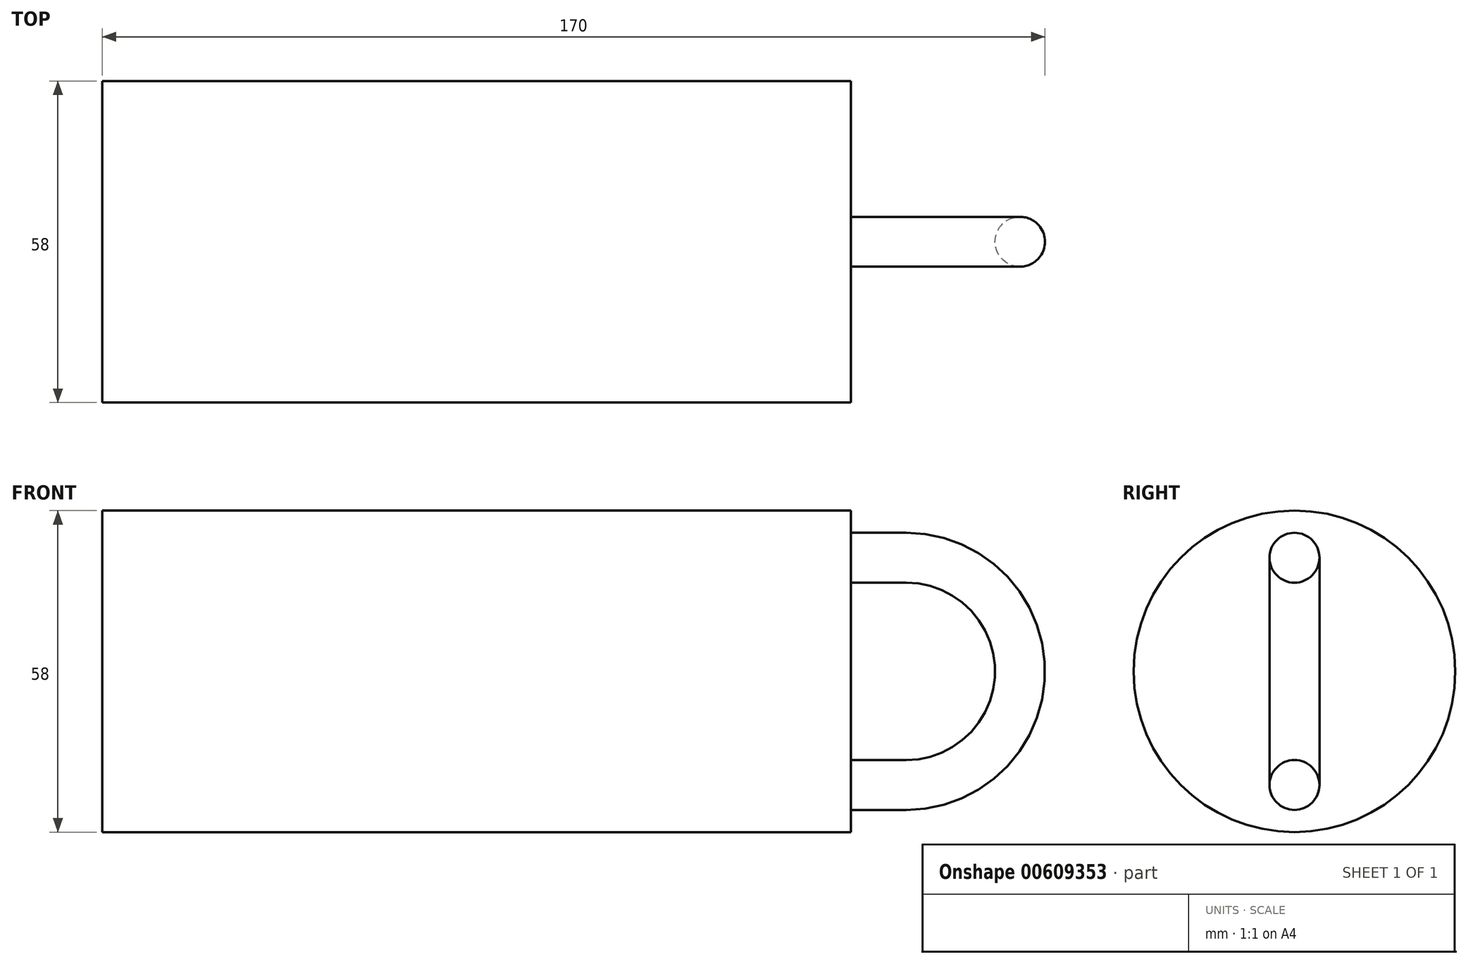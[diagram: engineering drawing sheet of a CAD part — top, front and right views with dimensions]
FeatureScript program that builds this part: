
annotation { "Feature Type Name" : "Feature", "Feature Type Description" : "" }
export const myFeature = defineFeature(function(context is Context, id is Id, definition is map)
    precondition{}
    {
        {
            var Q0;
            Q0=qCreatedBy(makeId("Right.planeOp"),FACE);
            var sketch = newSketch(context, id + "F0", { "sketchPlane" : qUnion([Q0])});
            skCircle(sketch, "E0", {"center": v(0, 0) * mm, "radius": 29 * mm});
            skSolve(sketch);
        }
        {
            var Q0;
            Q0 = qSketchRegion(id + "F0", true);
            extrude(context, id + "F1", {"entities" : qUnion([Q0]), "oppositeDirection" : true, "depth" : 135 * mm, "offsetDistance" : 25 * mm});
        }
        {
            var Q0;
            Q0=qCreatedBy(makeId("Right.planeOp"),FACE);
            var sketch = newSketch(context, id + "F2", { "sketchPlane" : qUnion([Q0])});
            skLineSegment(sketch, "E1", {"start": v(0, 0) * mm, "end": v(0, 20.5) * mm});
            skCircle(sketch, "E2", {"center": v(0, 20.5) * mm, "radius": 4.5 * mm});
            skLineSegment(sketch, "E3", {"start": v(0, 0) * mm, "end": v(-200, 0) * mm});
            skSolve(sketch);
        }
        {
            var Q0;
            Q0=makeQuery(id+"F2.imprint","IMPRINT",FACE,{"disambiguationData":[TD([[makeQuery(id+"F2.imprint","IMPRINT",EDGE,{"derivedFrom":sQuery(id+"F2.wireOp",EDGE,"E2")}),1.0]])]});
            var Q1;
            Q1=sQuery(id+"F2.wireOp",EDGE,"E3");
            revolve(context, id + "F3", {"operationType" : NewBodyOperationType.ADD, "entities" : qUnion([Q0]), "axis" : qUnion([Q1]), "revolveType" : RevolveType.FULL});
        }
        {
            var Q0;
            Q0=makeQuery(id+"F1.opExtrude","CAP_FACE",FACE,{"disambiguationData":[OSD([sQuery(id+"F0.wireOp",EDGE,"E0")])],"isStart":false});
            extrude(context, id + "F4", {"entities" : qUnion([Q0]), "operationType" : NewBodyOperationType.ADD, "depth" : 10 * mm, "offsetDistance" : 25 * mm});
        }
        {
            var Q0;
            Q0=makeQuery(id+"F1.opExtrude","CAP_FACE",FACE,{"disambiguationData":[OSD([sQuery(id+"F0.wireOp",EDGE,"E0")])],"isStart":true});
            extrude(context, id + "F5", {"entities" : qUnion([Q0]), "operationType" : NewBodyOperationType.REMOVE, "oppositeDirection" : true, "depth" : 10 * mm, "offsetDistance" : 25 * mm});
        }
    });
